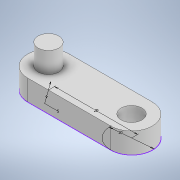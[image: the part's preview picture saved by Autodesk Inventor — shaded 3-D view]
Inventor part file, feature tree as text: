
AUTODESK INVENTOR PART (.ipt)
format: ipt  version: 2022 (Build 260153000, 153)  size: 111,104 bytes
history: native  units: mm
features: sketch x2, extrude x2
ambient origin geometry x8: Origin, YZ Plane, XZ Plane, XY Plane, X Axis, Y Axis, Z Axis, Center Point
bodies: Solid1 (feature_tree)
feature tree (4):
  sketch  "Sketch1"  dims[d0=20.0mm d1=10.0mm]
  extrude  "Extrusion1"  Depth=10.0mm
  extrude  "Extrusion3"  Depth=5.0mm TaperAngle=0.0deg
  sketch  "Sketch2"  dims[d2=5.0mm d4=5.0mm d5=0.0mm d8=5.0mm d9=0.0mm]
